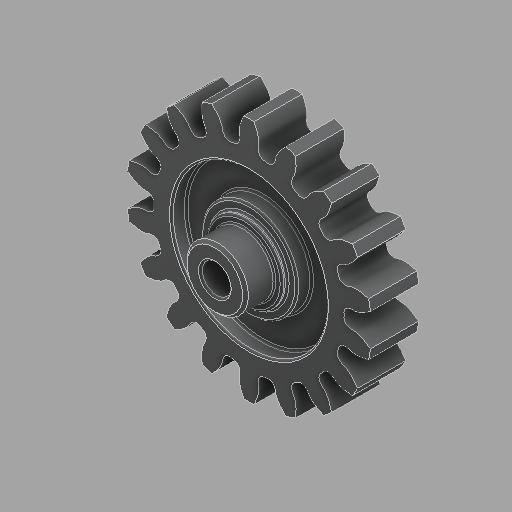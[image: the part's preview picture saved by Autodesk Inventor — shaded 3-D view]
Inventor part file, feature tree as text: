
AUTODESK INVENTOR PART (.ipt)
format: ipt  version: 2024.2 (Build 282272000, 272)  size: 443,392 bytes
history: native  units: in
note: dims shown in document units (in); Inventor stores cm internally (conversion verified against a paired STEP export)
features: chamfer x1
ambient origin geometry x8: Origin, YZ Plane, XZ Plane, XY Plane, X Axis, Y Axis, Z Axis, Center Point
bodies: Solid1 (feature_tree)
feature tree (1):
  chamfer  "Chamfer4"  [1 undecoded]
note: 1 required parameter value undecoded (feature->parameter linkage not recoverable at this tier; creation-order binding heuristic only, values carry confidence <= 0.55)
